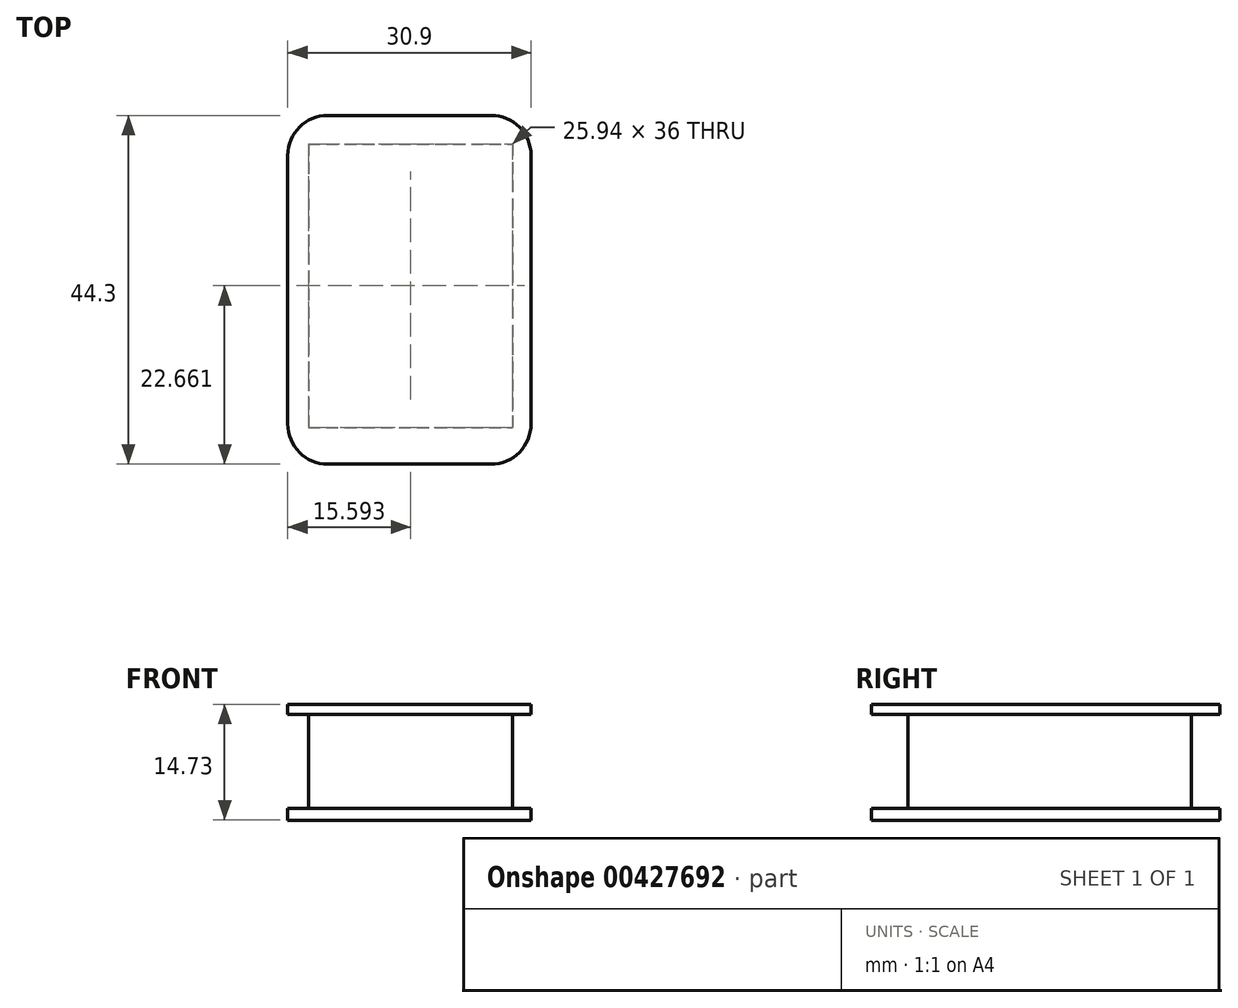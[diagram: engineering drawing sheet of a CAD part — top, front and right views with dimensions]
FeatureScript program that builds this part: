
annotation { "Feature Type Name" : "Feature", "Feature Type Description" : "" }
export const myFeature = defineFeature(function(context is Context, id is Id, definition is map)
    precondition{}
    {
        {
            var Q0;
            Q0=qCreatedBy(makeId("Top.planeOp"),FACE);
            var sketch = newSketch(context, id + "F0", { "sketchPlane" : qUnion([Q0])});
            skLineSegment(sketch, "E0.bottom", {"start": v(-13.4, 0) * mm, "end": v(12.53, 0) * mm});
            skLineSegment(sketch, "E0.top", {"start": v(-13.4, -36) * mm, "end": v(12.53, -36) * mm});
            skLineSegment(sketch, "E0.left", {"start": v(-13.4, 0) * mm, "end": v(-13.4, -36) * mm});
            skLineSegment(sketch, "E0.right", {"start": v(12.53, 0) * mm, "end": v(12.53, -36) * mm});
            skSolve(sketch);
        }
        {
            var Q0;
            Q0 = qSketchRegion(id + "F0", true);
            extrude(context, id + "F1", {"entities" : qUnion([Q0]), "depth" : 11.94 * mm});
        }
        {
            var Q0;
            Q0=makeQuery(id+"F1.opExtrude","CAP_FACE",FACE,{"disambiguationData":[OSD([sQuery(id+"F0.wireOp",EDGE,"E0.bottom"),sQuery(id+"F0.wireOp",EDGE,"E0.top"),sQuery(id+"F0.wireOp",EDGE,"E0.left"),sQuery(id+"F0.wireOp",EDGE,"E0.right")])],"isStart":false});
            var sketch = newSketch(context, id + "F2", { "sketchPlane" : qUnion([Q0])});
            skLineSegment(sketch, "E1.bottom", {"start": v(-16.03, 3.64) * mm, "end": v(14.87, 3.64) * mm});
            skLineSegment(sketch, "E1.top", {"start": v(-16.03, -40.66) * mm, "end": v(14.87, -40.66) * mm});
            skLineSegment(sketch, "E1.left", {"start": v(-16.03, 3.64) * mm, "end": v(-16.03, -40.66) * mm});
            skLineSegment(sketch, "E1.right", {"start": v(14.87, 3.64) * mm, "end": v(14.87, -40.66) * mm});
            skSolve(sketch);
        }
        {
            var Q0;
            Q0 = qSketchRegion(id + "F2", true);
            extrude(context, id + "F3", {"entities" : qUnion([Q0]), "operationType" : NewBodyOperationType.ADD, "depth" : 1.27 * mm});
        }
        {
            var Q0;
            Q0=makeQuery(id+"F1.opExtrude","CAP_FACE",FACE,{"disambiguationData":[OSD([sQuery(id+"F0.wireOp",EDGE,"E0.bottom"),sQuery(id+"F0.wireOp",EDGE,"E0.top"),sQuery(id+"F0.wireOp",EDGE,"E0.left"),sQuery(id+"F0.wireOp",EDGE,"E0.right")])],"isStart":true});
            var sketch = newSketch(context, id + "F4", { "sketchPlane" : qUnion([Q0])});
            skLineSegment(sketch, "E2.bottom", {"start": v(-16.03, 40.66) * mm, "end": v(14.87, 40.66) * mm});
            skLineSegment(sketch, "E2.top", {"start": v(-16.03, -3.64) * mm, "end": v(14.87, -3.64) * mm});
            skLineSegment(sketch, "E2.left", {"start": v(-16.03, 40.66) * mm, "end": v(-16.03, -3.64) * mm});
            skLineSegment(sketch, "E2.right", {"start": v(14.87, 40.66) * mm, "end": v(14.87, -3.64) * mm});
            skSolve(sketch);
        }
        {
            var Q0;
            Q0 = qSketchRegion(id + "F4", true);
            extrude(context, id + "F5", {"entities" : qUnion([Q0]), "operationType" : NewBodyOperationType.ADD, "depth" : 1.52 * mm});
        }
        {
            var Q0;
            Q0=makeQuery(id+"F5.opExtrude","SWEPT_EDGE",EDGE,{"disambiguationData":[OSD([sQuery(id+"F4.wireOp",EDGE,"E2.bottom"),sQuery(id+"F4.wireOp",EDGE,"E2.right")])]});
            var Q1;
            Q1=makeQuery(id+"F3.opExtrude","SWEPT_EDGE",EDGE,{"disambiguationData":[OSD([sQuery(id+"F2.wireOp",EDGE,"E1.top"),sQuery(id+"F2.wireOp",EDGE,"E1.right")])]});
            var Q2;
            Q2=makeQuery(id+"F5.opExtrude","SWEPT_EDGE",EDGE,{"disambiguationData":[OSD([sQuery(id+"F4.wireOp",EDGE,"E2.top"),sQuery(id+"F4.wireOp",EDGE,"E2.right")])]});
            var Q3;
            Q3=makeQuery(id+"F5.opExtrude","SWEPT_EDGE",EDGE,{"disambiguationData":[OSD([sQuery(id+"F4.wireOp",EDGE,"E2.bottom"),sQuery(id+"F4.wireOp",EDGE,"E2.left")])]});
            var Q4;
            Q4=makeQuery(id+"F3.opExtrude","SWEPT_EDGE",EDGE,{"disambiguationData":[OSD([sQuery(id+"F2.wireOp",EDGE,"E1.top"),sQuery(id+"F2.wireOp",EDGE,"E1.left")])]});
            var Q5;
            Q5=makeQuery(id+"F3.opExtrude","SWEPT_EDGE",EDGE,{"disambiguationData":[OSD([sQuery(id+"F2.wireOp",EDGE,"E1.bottom"),sQuery(id+"F2.wireOp",EDGE,"E1.right")])]});
            var Q6;
            Q6=makeQuery(id+"F3.opExtrude","SWEPT_EDGE",EDGE,{"disambiguationData":[OSD([sQuery(id+"F2.wireOp",EDGE,"E1.bottom"),sQuery(id+"F2.wireOp",EDGE,"E1.left")])]});
            var Q7;
            Q7=makeQuery(id+"F5.opExtrude","SWEPT_EDGE",EDGE,{"disambiguationData":[OSD([sQuery(id+"F4.wireOp",EDGE,"E2.top"),sQuery(id+"F4.wireOp",EDGE,"E2.left")])]});
            fillet(context, id + "F6", {"entities" : qUnion([Q0, Q1, Q2, Q3, Q4, Q5, Q6, Q7]), "radius" : 5.08 * mm, "tangentPropagation" : true, "allowEdgeOverflow" : false});
        }
    });
